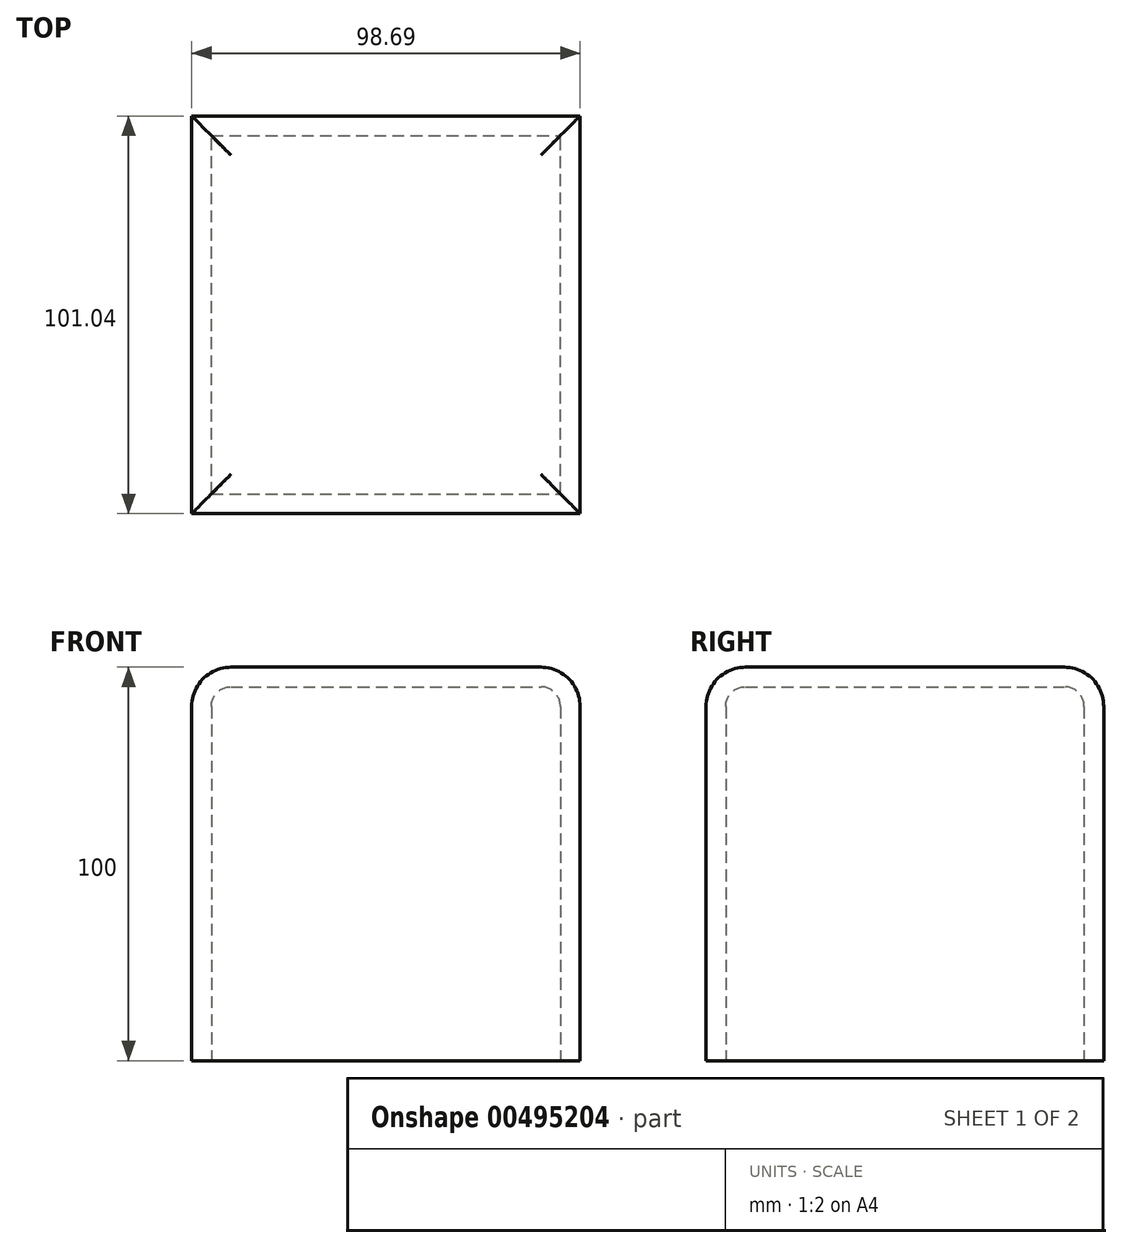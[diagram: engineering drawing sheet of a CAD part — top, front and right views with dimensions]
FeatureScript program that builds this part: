
annotation { "Feature Type Name" : "Feature", "Feature Type Description" : "" }
export const myFeature = defineFeature(function(context is Context, id is Id, definition is map)
    precondition{}
    {
        {
            var Q0;
            Q0=qCreatedBy(makeId("Top.planeOp"),FACE);
            var sketch = newSketch(context, id + "F0", { "sketchPlane" : qUnion([Q0])});
            skLineSegment(sketch, "E0.bottom", {"start": v(-63.64, -51.74) * mm, "end": v(35.05, -51.74) * mm});
            skLineSegment(sketch, "E0.top", {"start": v(-63.64, 49.3) * mm, "end": v(35.05, 49.3) * mm});
            skLineSegment(sketch, "E0.left", {"start": v(-63.64, -51.74) * mm, "end": v(-63.64, 49.3) * mm});
            skLineSegment(sketch, "E0.right", {"start": v(35.05, -51.74) * mm, "end": v(35.05, 49.3) * mm});
            skLineSegment(sketch, "E1.bottom", {"start": v(35.4, 49.5) * mm, "end": v(0, 49.5) * mm});
            skLineSegment(sketch, "E1.top", {"start": v(35.4, 94.68) * mm, "end": v(0, 94.68) * mm});
            skLineSegment(sketch, "E1.left", {"start": v(35.4, 49.5) * mm, "end": v(35.4, 94.68) * mm});
            skLineSegment(sketch, "E1.right", {"start": v(0, 49.5) * mm, "end": v(0, 94.68) * mm});
            skSolve(sketch);
        }
        {
            var Q0;
            Q0=makeQuery(id+"F0.imprint","IMPRINT",FACE,{"disambiguationData":[TD([[makeQuery(id+"F0.imprint","IMPRINT",EDGE,{"derivedFrom":sQuery(id+"F0.wireOp",EDGE,"E0.bottom")}),1.0]])]});
            extrude(context, id + "F1", {"entities" : qUnion([Q0]), "depth" : 100 * mm, "offsetDistance" : 25 * mm});
        }
        {
            var Q0;
            Q0=makeQuery(id+"F1.opExtrude","CAP_EDGE",EDGE,{"disambiguationData":[OSD([sQuery(id+"F0.wireOp",EDGE,"E0.bottom")])],"isStart":false});
            var Q1;
            Q1=makeQuery(id+"F1.opExtrude","CAP_EDGE",EDGE,{"disambiguationData":[OSD([sQuery(id+"F0.wireOp",EDGE,"E0.right")])],"isStart":false});
            var Q2;
            Q2=makeQuery(id+"F1.opExtrude","CAP_EDGE",EDGE,{"disambiguationData":[OSD([sQuery(id+"F0.wireOp",EDGE,"E0.top")])],"isStart":false});
            var Q3;
            Q3=makeQuery(id+"F1.opExtrude","CAP_EDGE",EDGE,{"disambiguationData":[OSD([sQuery(id+"F0.wireOp",EDGE,"E0.left")])],"isStart":false});
            fillet(context, id + "F2", {"entities" : qUnion([Q0, Q1, Q2, Q3]), "tangentPropagation" : true, "radius" : 10 * mm, "defaultsChanged" : false, "vertexSettings" : [], "allowEdgeOverflow" : false});
        }
        {
            var Q0;
            Q0=makeQuery(id+"F1.opExtrude","CAP_FACE",FACE,{"disambiguationData":[OSD([sQuery(id+"F0.wireOp",EDGE,"E0.bottom"),sQuery(id+"F0.wireOp",EDGE,"E0.top"),sQuery(id+"F0.wireOp",EDGE,"E0.left"),sQuery(id+"F0.wireOp",EDGE,"E0.right")])],"isStart":true});
            shell(context, id + "F3", {"entities" : qUnion([Q0]), "thickness" : 5 * mm});
        }
    });
